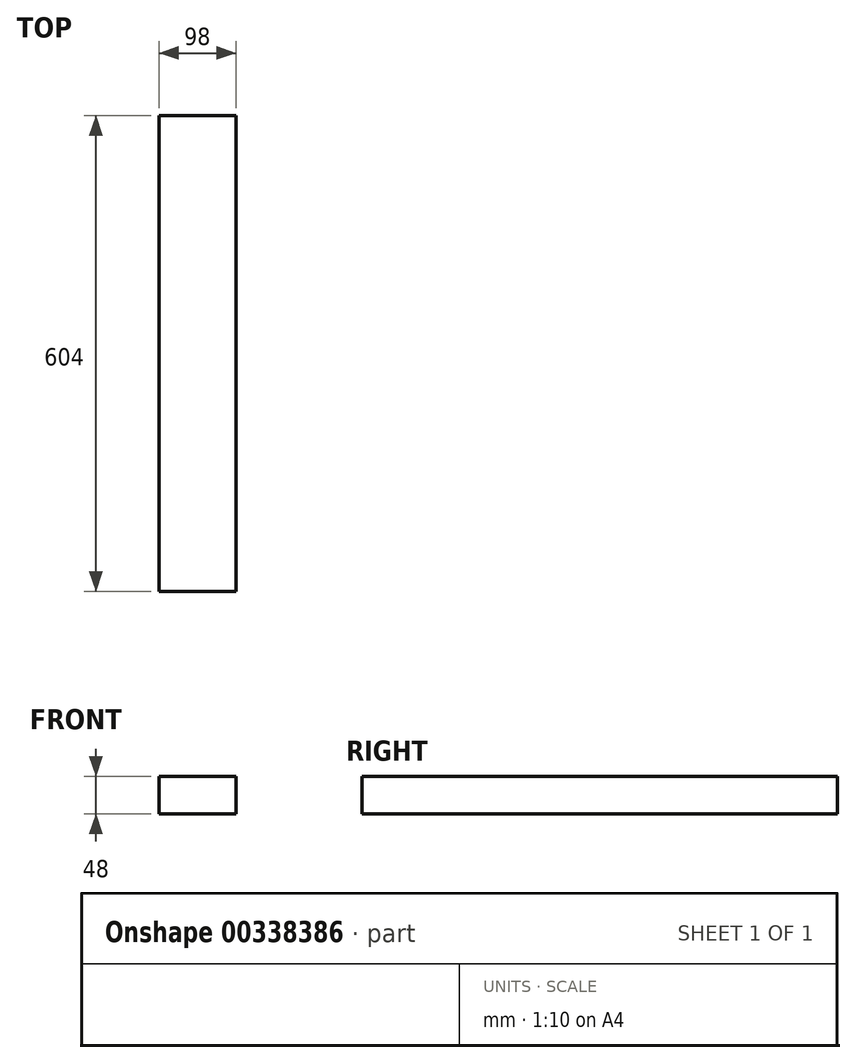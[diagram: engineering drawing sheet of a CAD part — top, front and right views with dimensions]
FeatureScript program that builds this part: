
annotation { "Feature Type Name" : "Feature", "Feature Type Description" : "" }
export const myFeature = defineFeature(function(context is Context, id is Id, definition is map)
    precondition{}
    {
        {
            var Q0;
            Q0=qCreatedBy(makeId("Front.planeOp"),FACE);
            var sketch = newSketch(context, id + "F0", { "sketchPlane" : qUnion([Q0])});
            skLineSegment(sketch, "E0.bottom", {"start": v(-49, -24) * mm, "end": v(49, -24) * mm});
            skLineSegment(sketch, "E0.top", {"start": v(-49, 24) * mm, "end": v(49, 24) * mm});
            skLineSegment(sketch, "E0.left", {"start": v(-49, -24) * mm, "end": v(-49, 24) * mm});
            skLineSegment(sketch, "E0.right", {"start": v(49, -24) * mm, "end": v(49, 24) * mm});
            skPoint(sketch, "E0.middle", {"position": v(0, 0) * mm});
            skSolve(sketch);
        }
        {
            var Q0;
            Q0=makeQuery(id+"F0.imprint","IMPRINT",FACE,{"disambiguationData":[TD([[makeQuery(id+"F0.imprint","IMPRINT",EDGE,{"derivedFrom":sQuery(id+"F0.wireOp",EDGE,"E0.bottom")}),1.0]])]});
            extrude(context, id + "F1", {"entities" : qUnion([Q0]), "offsetDistance" : 25 * mm, "depth" : 604 * mm});
        }
    });
